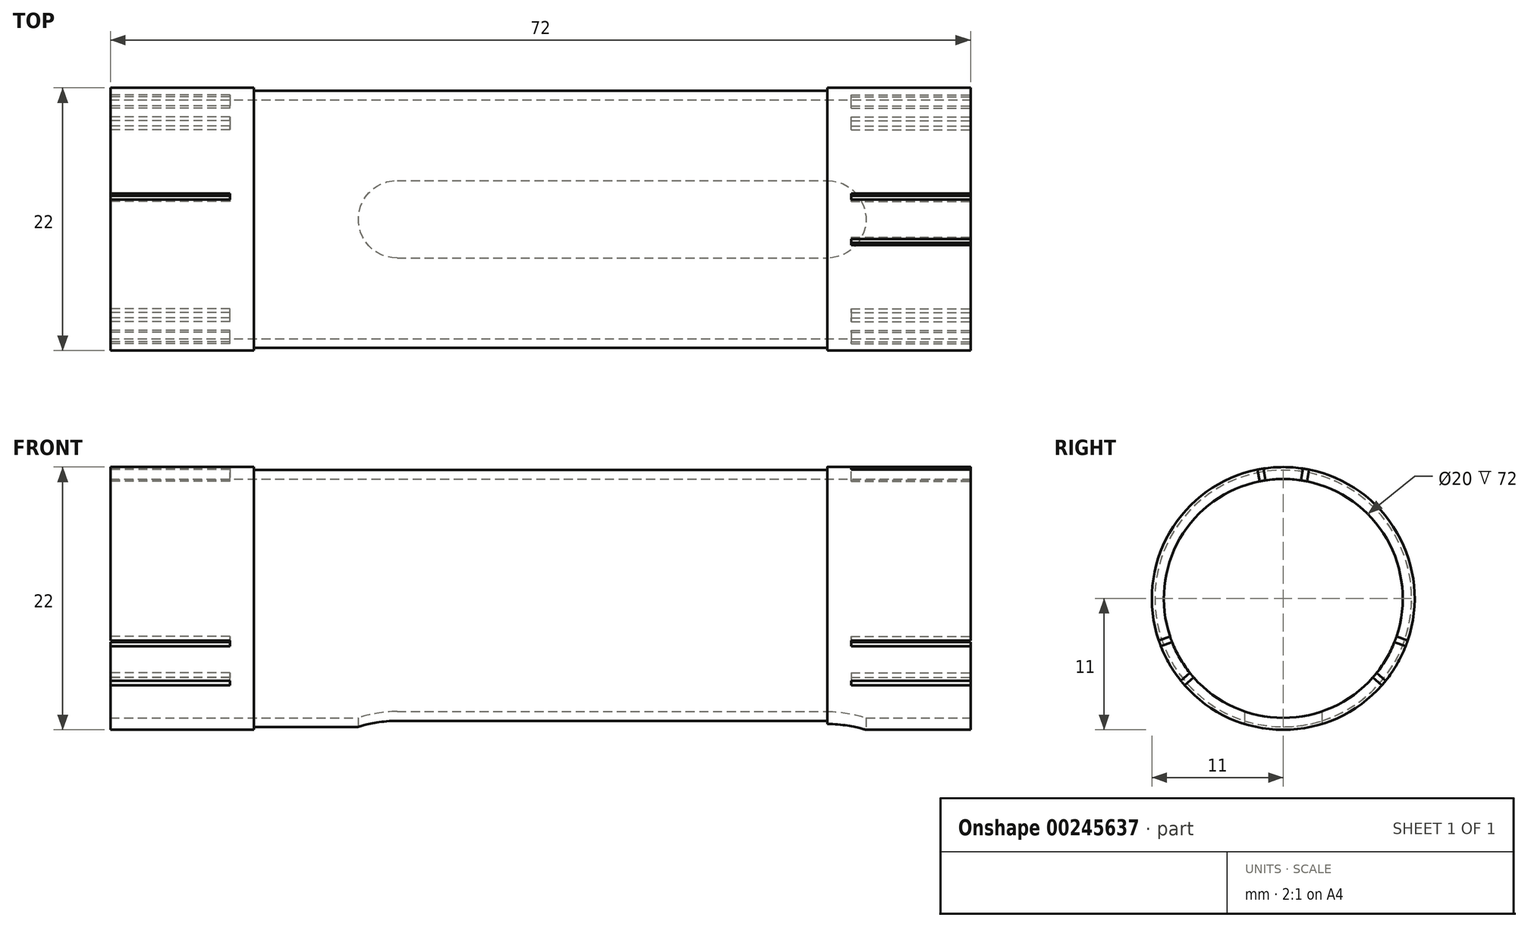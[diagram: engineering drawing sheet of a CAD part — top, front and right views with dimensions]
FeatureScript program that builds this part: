
annotation { "Feature Type Name" : "Feature", "Feature Type Description" : "" }
export const myFeature = defineFeature(function(context is Context, id is Id, definition is map)
    precondition{}
    {
        {
            var Q0;
            Q0=qCreatedBy(makeId("Right.planeOp"),FACE);
            var sketch = newSketch(context, id + "F0", { "sketchPlane" : qUnion([Q0])});
            skCircle(sketch, "E0", {"center": v(0, 0) * mm, "radius": 11 * mm});
            skSolve(sketch);
        }
        {
            var Q0;
            Q0=makeQuery(id+"F0.imprint","IMPRINT",FACE,{"disambiguationData":[TD([[makeQuery(id+"F0.imprint","IMPRINT",EDGE,{"derivedFrom":sQuery(id+"F0.wireOp",EDGE,"E0")}),1.0]])]});
            extrude(context, id + "F1", {"entities" : qUnion([Q0]), "depth" : 12 * mm});
        }
        {
            var Q0;
            Q0=makeQuery(id+"F1.opExtrude","CAP_FACE",FACE,{"disambiguationData":[OSD([sQuery(id+"F0.wireOp",EDGE,"E0")])],"isStart":false});
            var sketch = newSketch(context, id + "F2", { "sketchPlane" : qUnion([Q0])});
            skCircle(sketch, "E1", {"center": v(0, 0) * mm, "radius": 10.75 * mm});
            skSolve(sketch);
        }
        {
            var Q0;
            Q0=makeQuery(id+"F2.imprint","IMPRINT",FACE,{"disambiguationData":[TD([[makeQuery(id+"F2.imprint","IMPRINT",EDGE,{"derivedFrom":sQuery(id+"F2.wireOp",EDGE,"E1")}),1.0]])]});
            extrude(context, id + "F3", {"entities" : qUnion([Q0]), "operationType" : NewBodyOperationType.ADD, "depth" : (72 - 12 - 12) * mm});
        }
        {
            var Q0;
            Q0=makeQuery(id+"F3.opExtrude","CAP_FACE",FACE,{"disambiguationData":[OSD([sQuery(id+"F2.wireOp",EDGE,"E1")])],"isStart":false});
            var sketch = newSketch(context, id + "F4", { "sketchPlane" : qUnion([Q0])});
            skCircle(sketch, "E2", {"center": v(0, 0) * mm, "radius": 11 * mm});
            skSolve(sketch);
        }
        {
            var Q0;
            Q0=makeQuery(id+"F4.imprint","IMPRINT",FACE,{"disambiguationData":[TD([[makeQuery(id+"F4.imprint","IMPRINT",EDGE,{"derivedFrom":makeQuery(id+"F3.opExtrude","CAP_EDGE",EDGE,{"disambiguationData":[OSD([sQuery(id+"F2.wireOp",EDGE,"E1")])],"isStart":false})}),1.0]])]});
            var Q1;
            Q1=makeQuery(id+"F4.imprint","IMPRINT",FACE,{"disambiguationData":[TD([[makeQuery(id+"F4.imprint","IMPRINT",EDGE,{"derivedFrom":sQuery(id+"F4.wireOp",EDGE,"E2")}),1.0]])]});
            extrude(context, id + "F5", {"entities" : qUnion([Q0, Q1]), "operationType" : NewBodyOperationType.ADD, "depth" : 12 * mm});
        }
        {
            var Q0;
            Q0=makeQuery(id+"F1.opExtrude","CAP_FACE",FACE,{"disambiguationData":[OSD([sQuery(id+"F0.wireOp",EDGE,"E0")])],"isStart":true});
            var sketch = newSketch(context, id + "F6", { "sketchPlane" : qUnion([Q0])});
            skPoint(sketch, "E3", {"position": v(0, 0) * mm});
            skSolve(sketch);
        }
        {
            var Q0;
            Q0=sQuery(id+"F6.wireOp",VERTEX,"E3");
            var Q1;
            Q1=makeQuery(id+"F1.opExtrude","SWEPT_BODY",BODY,{"disambiguationData":[OSD([sQuery(id+"F0.wireOp",EDGE,"E0")])]});
            hole(context, id + "F7", {"style" : HoleStyle.SIMPLE, "endStyle" : HoleEndStyle.THROUGH, "holeDiameter" : 20 * mm, "tappedDepth" : 15 * mm, "tapClearance" : 0, "locations" : qUnion([Q0]), "scope" : qUnion([Q1]), "startStyle" : HoleStartStyle.SKETCH});
        }
        {
            var Q0;
            Q0=makeQuery(id+"F1.opExtrude","CAP_FACE",FACE,{"disambiguationData":[OSD([sQuery(id+"F0.wireOp",EDGE,"E0")])],"isStart":true});
            var sketch = newSketch(context, id + "F8", { "sketchPlane" : qUnion([Q0])});
            skLineSegment(sketch, "E4", {"start": v(0, 0) * mm, "end": v(0, 11) * mm, "construction": true});
            skLineSegment(sketch, "E5", {"start": v(0, 0) * mm, "end": v(9.53, -5.5) * mm, "construction": true});
            skLineSegment(sketch, "E6", {"start": v(0, 0) * mm, "end": v(-9.53, -5.5) * mm, "construction": true});
            skLineSegment(sketch, "E7", {"start": v(1.57, 10.37) * mm, "end": v(1.49, 9.89) * mm});
            skLineSegment(sketch, "E8", {"start": v(1.49, 9.89) * mm, "end": v(1.57, 10.37) * mm});
            skLineSegment(sketch, "E9", {"start": v(1.57, 10.37) * mm, "end": v(1.66, 10.87) * mm});
            skLineSegment(sketch, "E10", {"start": v(2.16, 10.78) * mm, "end": v(2.07, 10.28) * mm});
            skLineSegment(sketch, "E11", {"start": v(1.66, 10.87) * mm, "end": v(1.49, 9.89) * mm});
            skLineSegment(sketch, "E12", {"start": v(2.07, 10.28) * mm, "end": v(2.16, 10.78) * mm});
            skLineSegment(sketch, "E13", {"start": v(2.16, 10.78) * mm, "end": v(2, 9.8) * mm});
            skLineSegment(sketch, "E14.1.0", {"start": v(-10.25, -4) * mm, "end": v(-9.3, -3.65) * mm});
            skLineSegment(sketch, "E14.1.1", {"start": v(-10.42, -3.52) * mm, "end": v(-9.48, -3.18) * mm});
            skLineSegment(sketch, "E14.1.2", {"start": v(-9.3, -3.65) * mm, "end": v(-9.77, -3.82) * mm});
            skLineSegment(sketch, "E14.1.3", {"start": v(-9.94, -3.35) * mm, "end": v(-10.42, -3.52) * mm});
            skLineSegment(sketch, "E14.1.4", {"start": v(-9.77, -3.82) * mm, "end": v(-10.25, -4) * mm});
            skLineSegment(sketch, "E14.1.5", {"start": v(-9.77, -3.82) * mm, "end": v(-9.3, -3.65) * mm});
            skLineSegment(sketch, "E14.1.6", {"start": v(-9.77, -3.82) * mm, "end": v(-10.25, -4) * mm});
            skLineSegment(sketch, "E14.1.7", {"start": v(-10.42, -3.52) * mm, "end": v(-9.94, -3.35) * mm});
            skLineSegment(sketch, "E14.2.0", {"start": v(8.59, -6.88) * mm, "end": v(7.82, -6.23) * mm});
            skLineSegment(sketch, "E14.2.1", {"start": v(8.26, -7.27) * mm, "end": v(7.5, -6.62) * mm});
            skLineSegment(sketch, "E14.2.2", {"start": v(7.82, -6.23) * mm, "end": v(8.2, -6.55) * mm});
            skLineSegment(sketch, "E14.2.3", {"start": v(7.87, -6.93) * mm, "end": v(8.26, -7.27) * mm});
            skLineSegment(sketch, "E14.2.4", {"start": v(8.2, -6.55) * mm, "end": v(8.59, -6.88) * mm});
            skLineSegment(sketch, "E14.2.5", {"start": v(8.2, -6.55) * mm, "end": v(7.82, -6.23) * mm});
            skLineSegment(sketch, "E14.2.6", {"start": v(8.2, -6.55) * mm, "end": v(8.59, -6.88) * mm});
            skLineSegment(sketch, "E14.2.7", {"start": v(8.26, -7.27) * mm, "end": v(7.87, -6.93) * mm});
            skPoint(sketch, "E14.center", {"position": v(0, 0) * mm});
            skPoint(sketch, "E15", {"position": v(-1.82, 10.31) * mm});
            skLineSegment(sketch, "E16", {"start": v(-2.06, 10.27) * mm, "end": v(-2.16, 10.79) * mm});
            skLineSegment(sketch, "E17", {"start": v(-2.16, 10.79) * mm, "end": v(-1.98, 9.8) * mm});
            skLineSegment(sketch, "E18", {"start": v(-1.57, 10.36) * mm, "end": v(-1.66, 10.87) * mm});
            skLineSegment(sketch, "E19", {"start": v(-1.66, 10.87) * mm, "end": v(-1.49, 9.89) * mm});
            skPoint(sketch, "E20.1.0", {"position": v(-8.02, -6.73) * mm});
            skLineSegment(sketch, "E20.1.1", {"start": v(-8.26, -7.26) * mm, "end": v(-7.5, -6.62) * mm});
            skLineSegment(sketch, "E20.1.2", {"start": v(-8.59, -6.88) * mm, "end": v(-7.82, -6.23) * mm});
            skLineSegment(sketch, "E20.1.3", {"start": v(-8.18, -6.54) * mm, "end": v(-8.59, -6.88) * mm});
            skLineSegment(sketch, "E20.1.4", {"start": v(-7.86, -6.92) * mm, "end": v(-8.26, -7.26) * mm});
            skPoint(sketch, "E20.2.0", {"position": v(9.84, -3.58) * mm});
            skLineSegment(sketch, "E20.2.1", {"start": v(10.42, -3.53) * mm, "end": v(9.48, -3.18) * mm});
            skLineSegment(sketch, "E20.2.2", {"start": v(10.25, -4) * mm, "end": v(9.3, -3.65) * mm});
            skLineSegment(sketch, "E20.2.3", {"start": v(9.76, -3.82) * mm, "end": v(10.25, -4) * mm});
            skLineSegment(sketch, "E20.2.4", {"start": v(9.93, -3.35) * mm, "end": v(10.42, -3.53) * mm});
            skSolve(sketch);
        }
        {
            var Q0;
            {var subQ6=sQuery(id+"F8.wireOp",EDGE,"E17");var subQ8=makeQuery(id+"F8.imprint","IMPRINT",VERTEX,{"derivedFrom":subQ6});Q0=makeQuery(id+"F8.imprint","IMPRINT",FACE,{"disambiguationData":[TD([[makeQuery(id+"F8.imprint","IMPRINT",EDGE,{"disambiguationData":[TD([[subQ8,1.0]])],"derivedFrom":subQ6}),1.0]])]});}
            var Q1;
            {var subQ0=sQuery(id+"F8.wireOp",EDGE,"E11");Q1=makeQuery(id+"F8.imprint","IMPRINT",FACE,{"disambiguationData":[TD([[makeQuery(id+"F8.imprint","IMPRINT",EDGE,{"derivedFrom":subQ0}),1.0]])]});}
            var Q2;
            {var subQ3=sQuery(id+"F8.wireOp",EDGE,"E20.2.1");Q2=makeQuery(id+"F8.imprint","IMPRINT",FACE,{"disambiguationData":[TD([[makeQuery(id+"F8.imprint","IMPRINT",EDGE,{"derivedFrom":subQ3}),1.0]])]});}
            var Q3;
            {var subQ0=sQuery(id+"F8.wireOp",EDGE,"E14.2.1");Q3=makeQuery(id+"F8.imprint","IMPRINT",FACE,{"disambiguationData":[TD([[makeQuery(id+"F8.imprint","IMPRINT",EDGE,{"derivedFrom":subQ0}),-1.0]])]});}
            var Q4;
            {var subQ3=sQuery(id+"F8.wireOp",EDGE,"E20.1.1");Q4=makeQuery(id+"F8.imprint","IMPRINT",FACE,{"disambiguationData":[TD([[makeQuery(id+"F8.imprint","IMPRINT",EDGE,{"derivedFrom":subQ3}),1.0]])]});}
            var Q5;
            {var subQ0=sQuery(id+"F8.wireOp",EDGE,"E14.1.1");Q5=makeQuery(id+"F8.imprint","IMPRINT",FACE,{"disambiguationData":[TD([[makeQuery(id+"F8.imprint","IMPRINT",EDGE,{"derivedFrom":subQ0}),-1.0]])]});}
            extrude(context, id + "F9", {"entities" : qUnion([Q0, Q1, Q2, Q3, Q4, Q5]), "operationType" : NewBodyOperationType.REMOVE, "oppositeDirection" : true, "depth" : 10 * mm});
        }
        {
            var Q0;
            Q0=makeQuery(id+"F5.opExtrude","CAP_FACE",FACE,{"disambiguationData":[OSD([sQuery(id+"F4.wireOp",EDGE,"E2")])],"isStart":false});
            var sketch = newSketch(context, id + "F10", { "sketchPlane" : qUnion([Q0])});
            skPoint(sketch, "E21", {"position": v(1.49, 9.89) * mm});
            skPoint(sketch, "E22", {"position": v(1.98, 9.8) * mm});
            skLineSegment(sketch, "E23", {"start": v(1.49, 9.89) * mm, "end": v(1.66, 10.87) * mm});
            skLineSegment(sketch, "E24", {"start": v(1.98, 9.8) * mm, "end": v(2.16, 10.79) * mm});
            skLineSegment(sketch, "E25", {"start": v(-1.49, 9.89) * mm, "end": v(-1.66, 10.87) * mm});
            skLineSegment(sketch, "E26", {"start": v(-1.98, 9.8) * mm, "end": v(-2.16, 10.79) * mm});
            skLineSegment(sketch, "E27.1.0", {"start": v(-7.5, -6.62) * mm, "end": v(-8.26, -7.26) * mm});
            skLineSegment(sketch, "E27.1.1", {"start": v(-7.82, -6.23) * mm, "end": v(-8.59, -6.88) * mm});
            skLineSegment(sketch, "E27.1.2", {"start": v(-9.3, -3.65) * mm, "end": v(-10.25, -4) * mm});
            skPoint(sketch, "E27.1.3", {"position": v(-9.3, -3.65) * mm});
            skPoint(sketch, "E27.1.4", {"position": v(-9.48, -3.18) * mm});
            skLineSegment(sketch, "E27.1.5", {"start": v(-9.48, -3.18) * mm, "end": v(-10.42, -3.53) * mm});
            skLineSegment(sketch, "E27.2.0", {"start": v(9.48, -3.18) * mm, "end": v(10.42, -3.53) * mm});
            skLineSegment(sketch, "E27.2.1", {"start": v(9.3, -3.65) * mm, "end": v(10.25, -4) * mm});
            skLineSegment(sketch, "E27.2.2", {"start": v(7.82, -6.23) * mm, "end": v(8.59, -6.88) * mm});
            skPoint(sketch, "E27.2.3", {"position": v(7.82, -6.23) * mm});
            skPoint(sketch, "E27.2.4", {"position": v(7.5, -6.62) * mm});
            skLineSegment(sketch, "E27.2.5", {"start": v(7.5, -6.62) * mm, "end": v(8.26, -7.26) * mm});
            skPoint(sketch, "E27.center", {"position": v(0, 0) * mm});
            skSolve(sketch);
        }
        {
            var Q0;
            {var subQ0=sQuery(id+"F10.wireOp",EDGE,"E25");Q0=makeQuery(id+"F10.imprint","IMPRINT",FACE,{"disambiguationData":[TD([[makeQuery(id+"F10.imprint","IMPRINT",EDGE,{"derivedFrom":subQ0}),1.0]])]});}
            var Q1;
            {var subQ0=sQuery(id+"F10.wireOp",EDGE,"E23");Q1=makeQuery(id+"F10.imprint","IMPRINT",FACE,{"disambiguationData":[TD([[makeQuery(id+"F10.imprint","IMPRINT",EDGE,{"derivedFrom":subQ0}),-1.0]])]});}
            var Q2;
            {var subQ0=sQuery(id+"F10.wireOp",EDGE,"E27.2.0");Q2=makeQuery(id+"F10.imprint","IMPRINT",FACE,{"disambiguationData":[TD([[makeQuery(id+"F10.imprint","IMPRINT",EDGE,{"derivedFrom":subQ0}),-1.0]])]});}
            var Q3;
            {var subQ0=sQuery(id+"F10.wireOp",EDGE,"E27.2.2");Q3=makeQuery(id+"F10.imprint","IMPRINT",FACE,{"disambiguationData":[TD([[makeQuery(id+"F10.imprint","IMPRINT",EDGE,{"derivedFrom":subQ0}),-1.0]])]});}
            var Q4;
            {var subQ0=sQuery(id+"F10.wireOp",EDGE,"E27.1.2");Q4=makeQuery(id+"F10.imprint","IMPRINT",FACE,{"disambiguationData":[TD([[makeQuery(id+"F10.imprint","IMPRINT",EDGE,{"derivedFrom":subQ0}),-1.0]])]});}
            var Q5;
            {var subQ0=sQuery(id+"F10.wireOp",EDGE,"E27.1.0");Q5=makeQuery(id+"F10.imprint","IMPRINT",FACE,{"disambiguationData":[TD([[makeQuery(id+"F10.imprint","IMPRINT",EDGE,{"derivedFrom":subQ0}),-1.0]])]});}
            extrude(context, id + "F11", {"entities" : qUnion([Q0, Q1, Q2, Q3, Q4, Q5]), "operationType" : NewBodyOperationType.REMOVE, "oppositeDirection" : true, "depth" : 10 * mm});
        }
        {
            var Q0;
            Q0=qCreatedBy(makeId("Top.planeOp"),FACE);
            cPlane(context, id + "F12", {"entities" : qUnion([Q0]), "cplaneType" : CPlaneType.OFFSET, "offset" : 11 * mm, "oppositeDirection" : true, "width" : 150 * mm, "height" : 150 * mm});
        }
        {
            var Q0;
            Q0=qCreatedBy(id+"F12.planeOp",FACE);
            var sketch = newSketch(context, id + "F13", { "sketchPlane" : qUnion([Q0])});
            skLineSegment(sketch, "E28", {"start": v(60, -3.25) * mm, "end": v(24, -3.25) * mm});
            skLineSegment(sketch, "E29", {"start": v(24, 3.25) * mm, "end": v(60, 3.25) * mm});
            skArc(sketch, "E30", {"start": v(24, 3.25) * mm, "mid": v(20.75, 0) * mm, "end": v(24, -3.25) * mm});
            skArc(sketch, "E31", {"start": v(60, -3.25) * mm, "mid": v(63.25, 0) * mm, "end": v(60, 3.25) * mm});
            skSolve(sketch);
        }
        {
            var Q0;
            Q0=makeQuery(id+"F13.imprint","IMPRINT",FACE,{"disambiguationData":[TD([[makeQuery(id+"F13.imprint","IMPRINT",EDGE,{"derivedFrom":sQuery(id+"F13.wireOp",EDGE,"E28")}),-1.0]])]});
            extrude(context, id + "F14", {"entities" : qUnion([Q0]), "operationType" : NewBodyOperationType.REMOVE, "depth" : 5 * mm});
        }
    });
